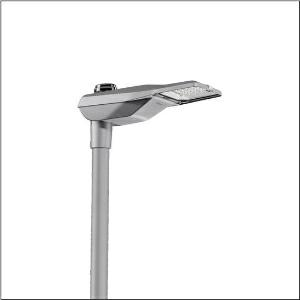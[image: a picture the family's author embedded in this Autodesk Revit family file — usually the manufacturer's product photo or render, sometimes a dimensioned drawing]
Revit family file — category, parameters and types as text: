
# Revit family: streetlight_sl_21_micro___st0_8a_5xe5c47n08cb_5e3b
name_source: partatom
category: Lighting Fixtures
units: mm (PartAtom-declared; Revit-internal decimal feet)

## family parameters
Cut with Voids When Loaded = No
Host = Face
Light Source = No
Part Type = Normal
Room Calculation Point = No
Round Connector Dimension = Use Diameter
Shared = No

## types (1)
- --- (1 x LED, 2380 lm, 15.8 W, 4000K)
    Apparent Load = 16 VA
    CIE Flux Codes = 38 75 97 100 100
    Color Rendering = 70
    Color Temperature = 4000K
    Default Elevation = 1800 mm
    Description = Streetlight SL 21 micro, mast luminaire, primary light control with lens, of PMMA, primary optical cover: cover, of toughened safety glass, transparent, light distribution: ST0.8a, light emission: direct distribution, primary light characteristic: asymmetric, installation type: post-top, LED, 3G 1.5mm², High Power LED, rated luminous flux: 2.380lm, luminous efficacy: 151lm/W, light colour: 740, colour temperature: 4000K, control: overheat protection, presetting dimming linear, constant luminous flux control, time-dependent luminous flux control, flexible luminous flux parameterisation, mains connection: 230..240V, AC, 50/60Hz, connection cable pre-assembled, cable length: 6,5m, wiring characteristics: H07RN-F, start of lifetime: 16W, end of service life: 16W, reduction: 8W, luminaire housing, of diecast aluminium (EN AC-44300), powder-coated, Siteco® metallic grey (DB 702S), corrosivity category C5 mid according to DIN EN ISO 12944, multi-level sealing system, sealing non-destructively replaceable, inclination adjustable: 0°, 5°, 10°, 15°, length: 528mm, width: 235mm, height: 110mm, spigot size: 76/60mm (post-top), protection rating (complete): IP66, insulation class (complete): insulation class I (protective earthing), certification: CE, ENEC, ENEC+, VDE, impact resistance: IK09, permissible operating ambient temperature for outdoor applications: -40..+50°C, standard-compliant lighting for roads and squares, packaging unit: 1 piece

Light Distribution: ST0.8a
    Height = 110 mm
    Lamp = 1 x LED
    Lamp Light Flux = 2380 lm
    Lamp Power = 15.8 W
    Lamp count = 1
    Length = 528 mm
    Luminous efficacy = 151 lm/W
    Manufacturer = Siteco
    ModVariant = No
    Model = 5XE5C47N08CB
    Number of Poles = 1
    OnlyDefault = Yes
    Power Factor = 1
    Product Name = Streetlight SL 21 micro | ST0.8a
    Product group = mast luminaire | pylon top
    ProductGroupID = 6100
    Protection Class = Protection class I
    Protection Degree = IP 66
    RLX_Detail_Level = 1
    RLX_Emergency_Light_Flux = 0 lm
    RLX_Emergency_Type = 0
    RLX_Emergency_Type_DB = No
    RlxData = <blob elided: 98029 chars, md5=21289c50>
    Socket = socket
    Standby Power = 0 W
    System Light Flux = 2380 lm
    System Power = 16 W
    Type Comments = factory setting: luminous flux: 100 % | dim-lin: 254 | 300 mA
    Type Image = l_1294375.jpg
    URL = http://relux.com
    VarID = @adj_083719
    Voltage = 0 V
    Weight = 0.00 kg
    Width = 235 mm

## geometry (parser evidence)
native form markers: Blend x4, Sweep x10
no freeform markers — native parametric forms only
